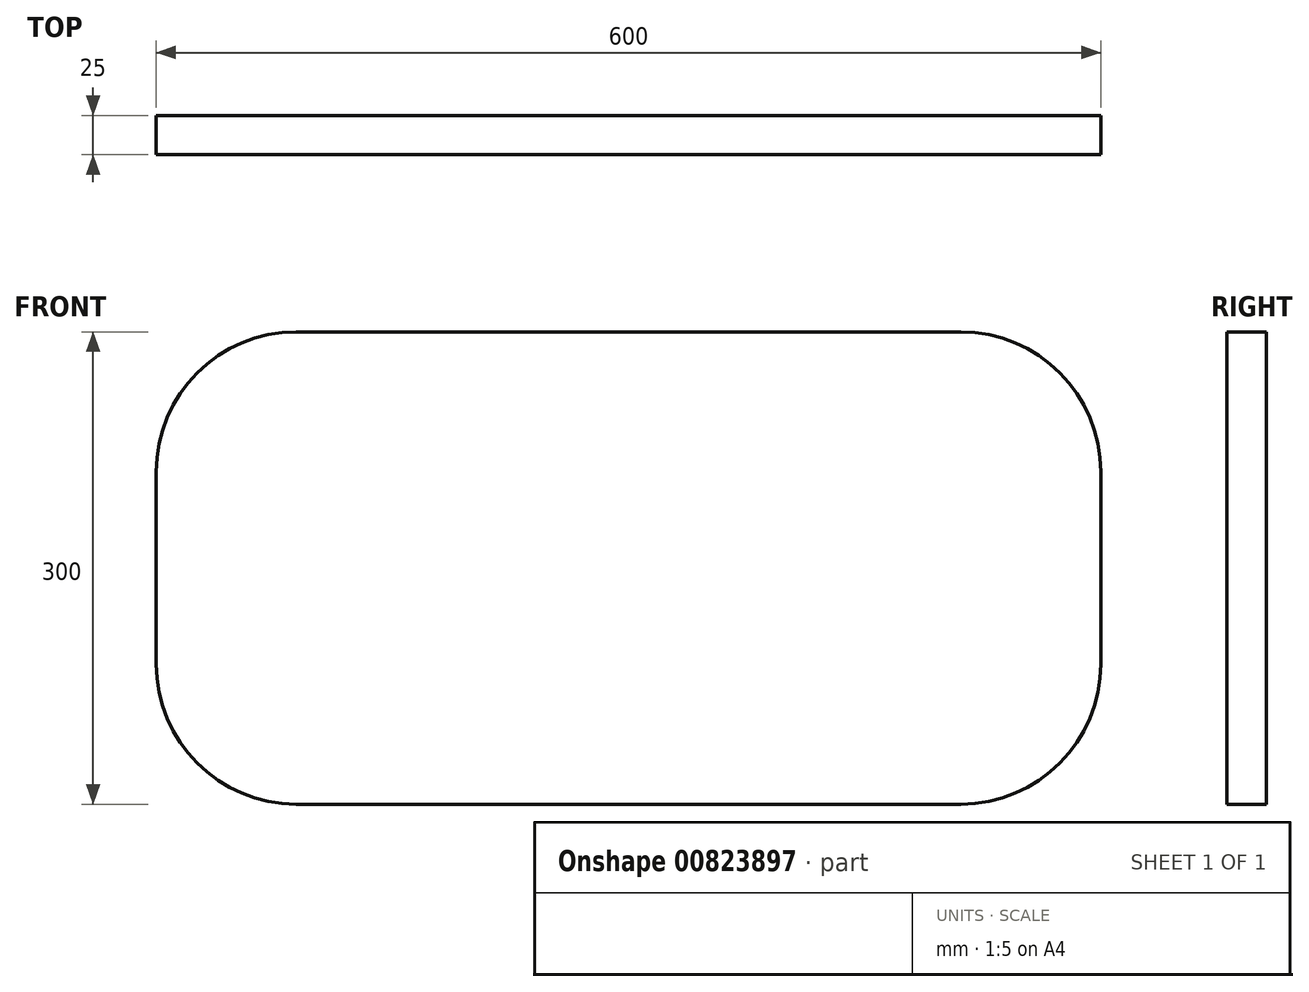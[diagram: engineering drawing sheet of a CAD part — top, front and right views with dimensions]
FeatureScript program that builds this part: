
annotation { "Feature Type Name" : "Feature", "Feature Type Description" : "" }
export const myFeature = defineFeature(function(context is Context, id is Id, definition is map)
    precondition{}
    {
        {
            var Q0;
            Q0=qCreatedBy(makeId("Front.planeOp"),FACE);
            var sketch = newSketch(context, id + "F0", { "sketchPlane" : qUnion([Q0])});
            skLineSegment(sketch, "E0.bottom", {"start": v(-211, 150) * mm, "end": v(211, 150) * mm});
            skLineSegment(sketch, "E0.top", {"start": v(-211, -150) * mm, "end": v(211, -150) * mm});
            skLineSegment(sketch, "E0.left", {"start": v(-300, 61) * mm, "end": v(-300, -61) * mm});
            skLineSegment(sketch, "E0.right", {"start": v(300, 61) * mm, "end": v(300, -61) * mm});
            skPoint(sketch, "E0.middle", {"position": v(0, 0) * mm});
            skPoint(sketch, "E1.visualSharp", {"position": v(-300, 150) * mm});
            skArc(sketch, "E1.filletArc", {"start": v(-211, 150) * mm, "mid": v(-273.93, 123.93) * mm, "end": v(-300, 61) * mm});
            skPoint(sketch, "E2.visualSharp", {"position": v(300, 150) * mm});
            skArc(sketch, "E2.filletArc", {"start": v(300, 61) * mm, "mid": v(273.93, 123.93) * mm, "end": v(211, 150) * mm});
            skPoint(sketch, "E3.visualSharp", {"position": v(300, -150) * mm});
            skArc(sketch, "E3.filletArc", {"start": v(211, -150) * mm, "mid": v(273.93, -123.93) * mm, "end": v(300, -61) * mm});
            skPoint(sketch, "E4.visualSharp", {"position": v(-300, -150) * mm});
            skArc(sketch, "E4.filletArc", {"start": v(-300, -61) * mm, "mid": v(-273.93, -123.93) * mm, "end": v(-211, -150) * mm});
            skSolve(sketch);
        }
        {
            var Q0;
            Q0=makeQuery(id+"F0.imprint","IMPRINT",FACE,{"disambiguationData":[TD([[makeQuery(id+"F0.imprint","IMPRINT",EDGE,{"derivedFrom":sQuery(id+"F0.wireOp",EDGE,"E0.bottom")}),-1.0]])]});
            extrude(context, id + "F1", {"entities" : qUnion([Q0]), "depth" : 25 * mm, "offsetDistance" : 25 * mm});
        }
    });
